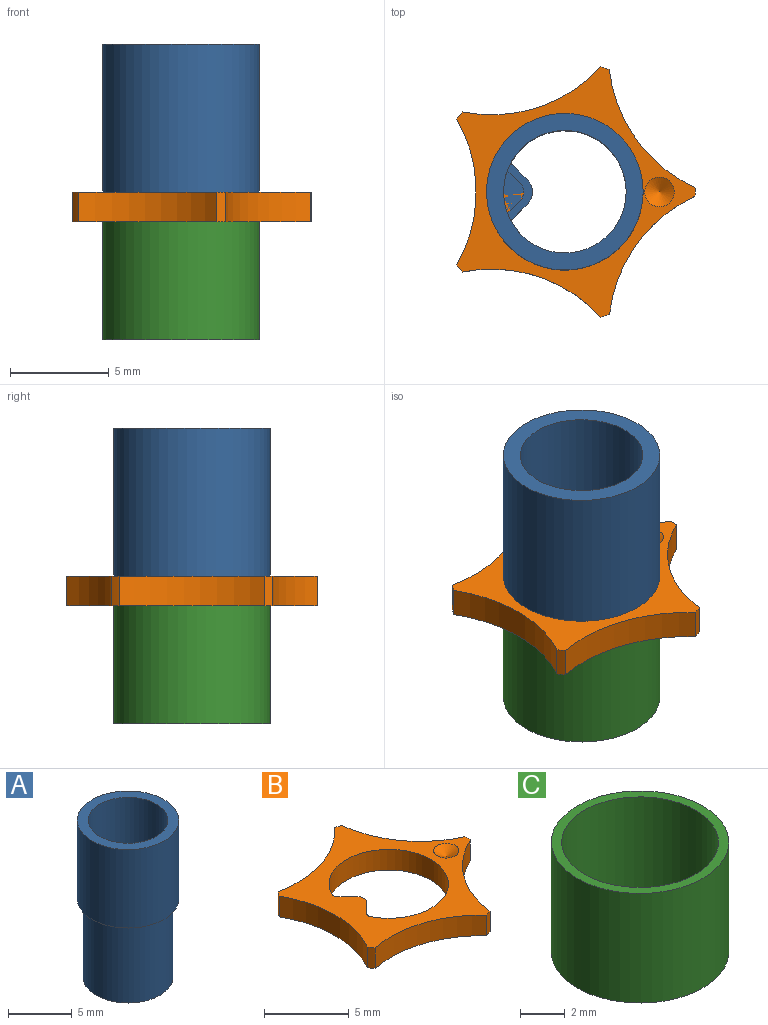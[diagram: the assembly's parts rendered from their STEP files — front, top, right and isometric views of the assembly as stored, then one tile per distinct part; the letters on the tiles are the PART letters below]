
ASSEMBLY  parts=3 mates=1
PART A: 12 faces, bbox 7.9x7.9x15 mm
  f0: cylinder r=3.11mm len=15mm, axis (0,0,-1), area 268.3mm2, adj f2,f4,f6,f7,f11
  f1: cylinder r=3.97mm len=7.94mm, axis (0,0,-1), area 187.1mm2, adj f2,f3
  f2: plane 7.94x7.94mm, normal (0,0,1), area 19.2mm2, adj f0,f1
  f3: plane 7.94x7.94mm, normal (0,0,-1), area 10.8mm2, adj f1,f10
  f4: plane 3.13x1.46mm, normal (0,0,1), area 2.7mm2, adj f0,f5,f6,f7,f8,f9
  f5: plane 7.5x0.75mm, normal (0.71,-0.71,0), area 7.9mm2, adj f4,f6,f9,f11
  f6: cylinder r=0.15mm len=7.5mm, axis (0,0,1), area 1.5mm2, adj f0,f4,f5,f11
  f7: cylinder r=0.15mm len=7.5mm, axis (0,0,1), area 1.5mm2, adj f0,f4,f8,f11
  f8: plane 7.5x0.75mm, normal (0.71,0.71,0), area 7.9mm2, adj f4,f7,f9,f11
  f9: cylinder r=0.9mm len=7.5mm, axis (0,0,1), area 10.6mm2, adj f4,f5,f8,f11
  f10: cylinder r=3.51mm len=7.5mm, axis (0,0,1), area 165.4mm2, adj f3,f11
  f11: plane 7.02x7.02mm, normal (0,0,-1), area 11mm2, adj f0,f5,f6,f7,f8,f9,f10
PART B: 19 faces, bbox 12.1x12.7x1.5 mm
  f0: cylinder r=7.5mm len=7.03mm, axis (0,0,-1), area 11.6mm2, adj f1,f15,f16,f17
  f1: cylinder r=6.6mm len=1.5mm, axis (0,0,-1), area 0.7mm2, adj f0,f2,f16,f17
  f2: cylinder r=7.5mm len=7.39mm, axis (0,0,-1), area 11.6mm2, adj f1,f3,f16,f17
  f3: cylinder r=6.6mm len=1.5mm, axis (0,0,-1), area 0.7mm2, adj f2,f4,f16,f17
  f4: cylinder r=7.5mm len=7.02mm, axis (0,0,-1), area 11.6mm2, adj f3,f5,f16,f17
  f5: cylinder r=6.6mm len=1.5mm, axis (0,0,-1), area 0.7mm2, adj f4,f6,f16,f17
  f6: cylinder r=7.5mm len=5.97mm, axis (0,0,-1), area 11.6mm2, adj f5,f7,f16,f17
  f7: cylinder r=6.6mm len=1.5mm, axis (0,0,-1), area 0.7mm2, adj f6,f8,f16,f17
  f8: cylinder r=7.5mm len=5.98mm, axis (0,0,-1), area 11.6mm2, adj f7,f15,f16,f17
  f9: cylinder r=3.53mm len=7.06mm, axis (0,0,-1), area 28.3mm2, adj f10,f14,f16,f17
  f10: cylinder r=0.3mm len=1.5mm, axis (0,0,-1), area 0.6mm2, adj f9,f11,f16,f17
  f11: plane 1.5x0.83mm, normal (0.71,-0.71,0), area 1.8mm2, adj f10,f12,f16,f17
  f12: cylinder r=0.6mm len=1.5mm, axis (0,0,-1), area 1.4mm2, adj f11,f13,f16,f17
  f13: plane 1.5x0.83mm, normal (0.71,0.71,0), area 1.8mm2, adj f12,f14,f16,f17
  f14: cylinder r=0.3mm len=1.5mm, axis (0,0,-1), area 0.6mm2, adj f9,f13,f16,f17
  f15: cylinder r=6.6mm len=1.5mm, axis (0,0,-1), area 0.7mm2, adj f0,f8,f16,f17
  f16: plane 12.69x12.07mm, normal (0,0,1), area 45.8mm2, adj f0,f1,f2,f3,f4,f5,f6,f7
  f17: plane 12.69x12.07mm, normal (0,0,-1), area 47.6mm2, adj f0,f1,f2,f3,f4,f5,f6,f7
  f18: cone r=0.75mm half-angle=60deg, axis (0,0,1), area 2mm2, adj f16
PART C: 4 faces, bbox 7.9x7.9x6 mm
  f0: cylinder r=3.51mm len=7.02mm, axis (0,0,-1), area 132.3mm2, adj f2,f3
  f1: cylinder r=3.97mm len=7.94mm, axis (0,0,-1), area 149.7mm2, adj f2,f3
  f2: plane 7.94x7.94mm, normal (0,0,1), area 10.8mm2, adj f0,f1
  f3: plane 7.94x7.94mm, normal (0,0,-1), area 10.8mm2, adj f0,f1
PLACE A at identity fixed
PLACE B t=(0,0,-1.5)mm
PLACE C t=(0,0,-7.5)mm
MATE fastened B.f1 <-> C.f0  axis (0,0,-1) through (0,0,-1.5)mm
